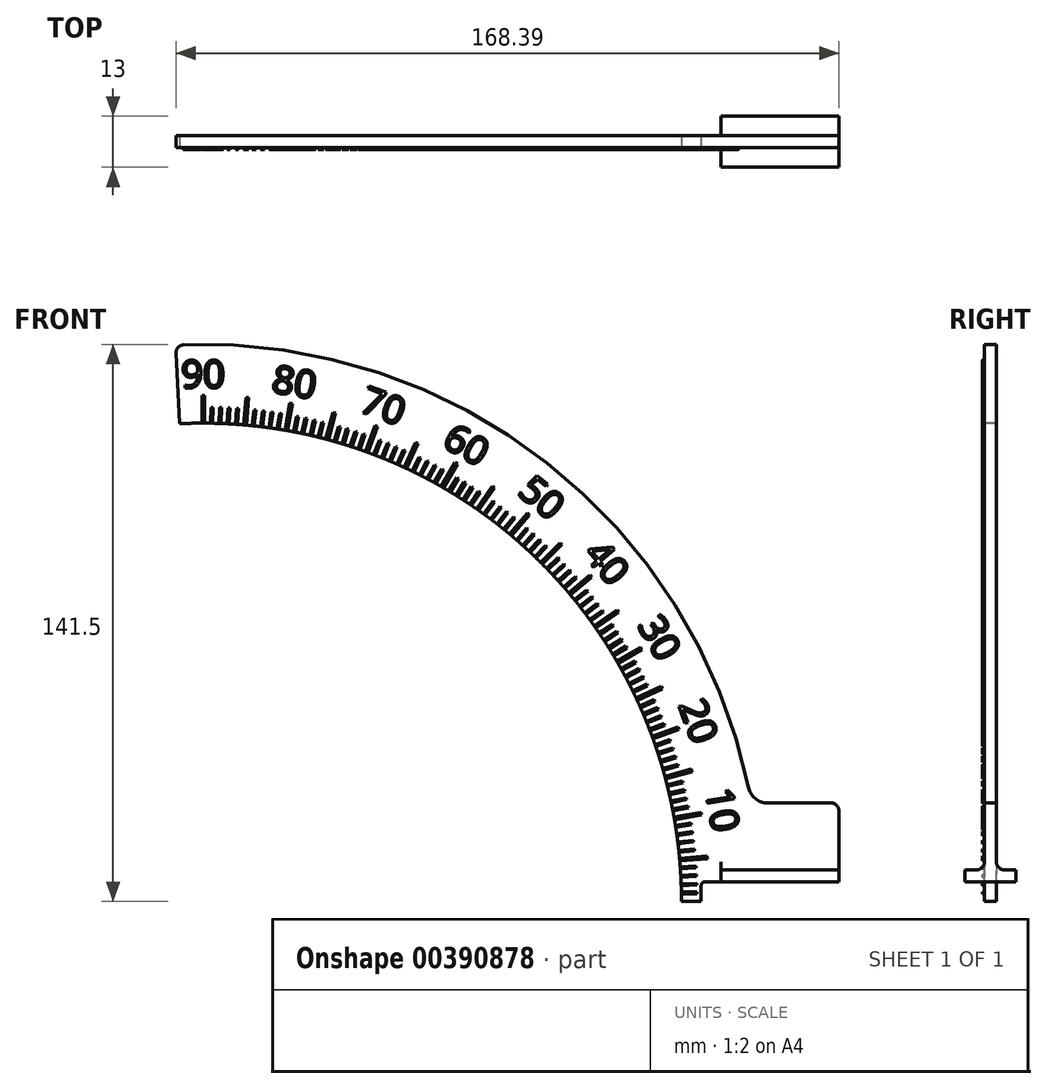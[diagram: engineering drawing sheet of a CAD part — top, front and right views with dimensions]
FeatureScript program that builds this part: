
annotation { "Feature Type Name" : "Feature", "Feature Type Description" : "" }
export const myFeature = defineFeature(function(context is Context, id is Id, definition is map)
    precondition{}
    {
        {
            var Q0;
            Q0=qCreatedBy(makeId("Front.planeOp"),FACE);
            var sketch = newSketch(context, id + "F0", { "sketchPlane" : qUnion([Q0])});
            skPoint(sketch, "E0", {"position": v(121.5, 0) * mm});
            skArc(sketch, "E1", {"start": v(121.5, 0) * mm, "mid": v(85.91, 85.91) * mm, "end": v(0, 121.5) * mm});
            skPoint(sketch, "E2", {"position": v(0, 121.5) * mm});
            skArc(sketch, "E3", {"start": v(0, 121.5) * mm, "mid": v(-3, 121.46) * mm, "end": v(-6, 121.35) * mm});
            skLineSegment(sketch, "E4", {"start": v(0, 0) * mm, "end": v(-6, 121.35) * mm, "construction": true});
            skLineSegment(sketch, "E5", {"start": v(-6, 121.35) * mm, "end": v(-6.89, 139.32) * mm, "construction": true});
            skLineSegment(sketch, "E6", {"start": v(121.5, 0) * mm, "end": v(171.8, 0) * mm});
            skLineSegment(sketch, "E7", {"start": v(0, 121.5) * mm, "end": v(0, 0) * mm, "construction": true});
            skLineSegment(sketch, "E8", {"start": v(0, 121.5) * mm, "end": v(0, 128.5) * mm, "construction": true});
            skPoint(sketch, "E9", {"position": v(0, 128.5) * mm});
            skLineSegment(sketch, "E10", {"start": v(-0.35, 121.5) * mm, "end": v(-0.35, 128.5) * mm});
            skLineSegment(sketch, "E11", {"start": v(-0.35, 128.5) * mm, "end": v(0.35, 128.5) * mm});
            skLineSegment(sketch, "E12", {"start": v(0.35, 128.5) * mm, "end": v(0.35, 121.5) * mm});
            skLineSegment(sketch, "E13", {"start": v(121.5, 0) * mm, "end": v(126.5, 0) * mm});
            skLineSegment(sketch, "E14", {"start": v(126.5, 0) * mm, "end": v(126.5, 4) * mm, "construction": true});
            skLineSegment(sketch, "E15", {"start": v(127.5, 5) * mm, "end": v(161.5, 5) * mm, "construction": true});
            skLineSegment(sketch, "E16", {"start": v(161.5, 5) * mm, "end": v(161.5, 23) * mm, "construction": true});
            skLineSegment(sketch, "E17", {"start": v(159.5, 25) * mm, "end": v(143.4, 25) * mm});
            skArc(sketch, "E18", {"start": v(-4.96, 141.41) * mm, "mid": v(87.29, 111.37) * mm, "end": v(138.5, 28.98) * mm, "construction": true});
            skLineSegment(sketch, "E19", {"start": v(0, 0) * mm, "end": v(121.5, 0) * mm, "construction": true});
            skPoint(sketch, "E20", {"position": v(0, 130.5) * mm});
            skPoint(sketch, "E21.1.0", {"position": v(11.37, 130) * mm});
            skLineSegment(sketch, "E21.1.1", {"start": v(10.85, 128.04) * mm, "end": v(11.55, 127.98) * mm});
            skLineSegment(sketch, "E21.1.2", {"start": v(10.24, 121.07) * mm, "end": v(10.85, 128.04) * mm});
            skLineSegment(sketch, "E21.1.3", {"start": v(11.55, 127.98) * mm, "end": v(10.94, 121) * mm});
            skPoint(sketch, "E21.2.0", {"position": v(22.66, 128.52) * mm});
            skLineSegment(sketch, "E21.2.1", {"start": v(21.97, 126.6) * mm, "end": v(22.66, 126.49) * mm});
            skLineSegment(sketch, "E21.2.2", {"start": v(20.75, 119.71) * mm, "end": v(21.97, 126.6) * mm});
            skLineSegment(sketch, "E21.2.3", {"start": v(22.66, 126.49) * mm, "end": v(21.44, 119.6) * mm});
            skPoint(sketch, "E21.3.0", {"position": v(33.78, 126.05) * mm});
            skLineSegment(sketch, "E21.3.1", {"start": v(32.92, 124.21) * mm, "end": v(33.6, 124.03) * mm});
            skLineSegment(sketch, "E21.3.2", {"start": v(31.1, 117.45) * mm, "end": v(32.92, 124.21) * mm});
            skLineSegment(sketch, "E21.3.3", {"start": v(33.6, 124.03) * mm, "end": v(31.78, 117.27) * mm});
            skPoint(sketch, "E21.4.0", {"position": v(44.63, 122.63) * mm});
            skLineSegment(sketch, "E21.4.1", {"start": v(43.62, 120.87) * mm, "end": v(44.28, 120.63) * mm});
            skLineSegment(sketch, "E21.4.2", {"start": v(41.23, 114.3) * mm, "end": v(43.62, 120.87) * mm});
            skLineSegment(sketch, "E21.4.3", {"start": v(44.28, 120.63) * mm, "end": v(41.88, 114.05) * mm});
            skPoint(sketch, "E21.5.0", {"position": v(55.15, 118.27) * mm});
            skLineSegment(sketch, "E21.5.1", {"start": v(53.99, 116.6) * mm, "end": v(54.62, 116.31) * mm});
            skLineSegment(sketch, "E21.5.2", {"start": v(51.03, 110.26) * mm, "end": v(53.99, 116.6) * mm});
            skLineSegment(sketch, "E21.5.3", {"start": v(54.62, 116.31) * mm, "end": v(51.67, 109.97) * mm});
            skPoint(sketch, "E21.6.0", {"position": v(65.25, 113.02) * mm});
            skLineSegment(sketch, "E21.6.1", {"start": v(63.95, 111.46) * mm, "end": v(64.55, 111.1) * mm});
            skLineSegment(sketch, "E21.6.2", {"start": v(60.45, 105.4) * mm, "end": v(63.95, 111.46) * mm});
            skLineSegment(sketch, "E21.6.3", {"start": v(64.55, 111.1) * mm, "end": v(61.05, 105.05) * mm});
            skPoint(sketch, "E21.7.0", {"position": v(74.85, 106.9) * mm});
            skLineSegment(sketch, "E21.7.1", {"start": v(73.42, 105.46) * mm, "end": v(74, 105.06) * mm});
            skLineSegment(sketch, "E21.7.2", {"start": v(69.4, 99.73) * mm, "end": v(73.42, 105.46) * mm});
            skLineSegment(sketch, "E21.7.3", {"start": v(74, 105.06) * mm, "end": v(69.98, 99.33) * mm});
            skPoint(sketch, "E21.8.0", {"position": v(83.88, 99.97) * mm});
            skLineSegment(sketch, "E21.8.1", {"start": v(82.33, 98.66) * mm, "end": v(82.87, 98.21) * mm});
            skLineSegment(sketch, "E21.8.2", {"start": v(77.83, 93.3) * mm, "end": v(82.33, 98.66) * mm});
            skLineSegment(sketch, "E21.8.3", {"start": v(82.87, 98.21) * mm, "end": v(78.37, 92.85) * mm});
            skPoint(sketch, "E21.9.0", {"position": v(92.28, 92.28) * mm});
            skLineSegment(sketch, "E21.9.1", {"start": v(90.62, 91.11) * mm, "end": v(91.11, 90.62) * mm});
            skLineSegment(sketch, "E21.9.2", {"start": v(85.67, 86.16) * mm, "end": v(90.62, 91.11) * mm});
            skLineSegment(sketch, "E21.9.3", {"start": v(91.11, 90.62) * mm, "end": v(86.16, 85.67) * mm});
            skPoint(sketch, "E21.10.0", {"position": v(99.97, 83.88) * mm});
            skLineSegment(sketch, "E21.10.1", {"start": v(98.21, 82.87) * mm, "end": v(98.66, 82.33) * mm});
            skLineSegment(sketch, "E21.10.2", {"start": v(92.85, 78.37) * mm, "end": v(98.21, 82.87) * mm});
            skLineSegment(sketch, "E21.10.3", {"start": v(98.66, 82.33) * mm, "end": v(93.3, 77.83) * mm});
            skPoint(sketch, "E21.11.0", {"position": v(106.9, 74.85) * mm});
            skLineSegment(sketch, "E21.11.1", {"start": v(105.06, 74) * mm, "end": v(105.46, 73.42) * mm});
            skLineSegment(sketch, "E21.11.2", {"start": v(99.33, 69.98) * mm, "end": v(105.06, 74) * mm});
            skLineSegment(sketch, "E21.11.3", {"start": v(105.46, 73.42) * mm, "end": v(99.73, 69.4) * mm});
            skPoint(sketch, "E21.12.0", {"position": v(113.02, 65.25) * mm});
            skLineSegment(sketch, "E21.12.1", {"start": v(111.1, 64.55) * mm, "end": v(111.46, 63.95) * mm});
            skLineSegment(sketch, "E21.12.2", {"start": v(105.05, 61.05) * mm, "end": v(111.1, 64.55) * mm});
            skLineSegment(sketch, "E21.12.3", {"start": v(111.46, 63.95) * mm, "end": v(105.4, 60.45) * mm});
            skPoint(sketch, "E21.13.0", {"position": v(118.27, 55.15) * mm});
            skLineSegment(sketch, "E21.13.1", {"start": v(116.31, 54.62) * mm, "end": v(116.6, 53.99) * mm});
            skLineSegment(sketch, "E21.13.2", {"start": v(109.97, 51.67) * mm, "end": v(116.31, 54.62) * mm});
            skLineSegment(sketch, "E21.13.3", {"start": v(116.6, 53.99) * mm, "end": v(110.26, 51.03) * mm});
            skPoint(sketch, "E21.14.0", {"position": v(122.63, 44.63) * mm});
            skLineSegment(sketch, "E21.14.1", {"start": v(120.63, 44.28) * mm, "end": v(120.87, 43.62) * mm});
            skLineSegment(sketch, "E21.14.2", {"start": v(114.05, 41.88) * mm, "end": v(120.63, 44.28) * mm});
            skLineSegment(sketch, "E21.14.3", {"start": v(120.87, 43.62) * mm, "end": v(114.3, 41.23) * mm});
            skPoint(sketch, "E21.15.0", {"position": v(126.05, 33.78) * mm});
            skLineSegment(sketch, "E21.15.1", {"start": v(124.03, 33.6) * mm, "end": v(124.21, 32.92) * mm});
            skLineSegment(sketch, "E21.15.2", {"start": v(117.27, 31.78) * mm, "end": v(124.03, 33.6) * mm});
            skLineSegment(sketch, "E21.15.3", {"start": v(124.21, 32.92) * mm, "end": v(117.45, 31.1) * mm});
            skPoint(sketch, "E21.16.0", {"position": v(128.52, 22.66) * mm});
            skLineSegment(sketch, "E21.16.1", {"start": v(126.49, 22.66) * mm, "end": v(126.6, 21.97) * mm});
            skLineSegment(sketch, "E21.16.2", {"start": v(119.6, 21.44) * mm, "end": v(126.49, 22.66) * mm});
            skLineSegment(sketch, "E21.16.3", {"start": v(126.6, 21.97) * mm, "end": v(119.71, 20.75) * mm});
            skPoint(sketch, "E21.17.0", {"position": v(130, 11.37) * mm});
            skLineSegment(sketch, "E21.17.1", {"start": v(127.98, 11.55) * mm, "end": v(128.04, 10.85) * mm});
            skLineSegment(sketch, "E21.17.2", {"start": v(121, 10.94) * mm, "end": v(127.98, 11.55) * mm});
            skLineSegment(sketch, "E21.17.3", {"start": v(128.04, 10.85) * mm, "end": v(121.07, 10.24) * mm});
            skPoint(sketch, "E21.18.0", {"position": v(130.5, 0) * mm});
            skLineSegment(sketch, "E21.anchor1", {"start": v(0, 0) * mm, "end": v(0, 130.5) * mm, "construction": true});
            skLineSegment(sketch, "E21.anchor2", {"start": v(0, 0) * mm, "end": v(130.5, 0) * mm, "construction": true});
            skLineSegment(sketch, "E22", {"start": v(0.25, 121.5) * mm, "end": v(0.25, 125.5) * mm});
            skLineSegment(sketch, "E23", {"start": v(0.25, 125.5) * mm, "end": v(-0.25, 125.5) * mm});
            skLineSegment(sketch, "E24", {"start": v(-0.25, 125.5) * mm, "end": v(-0.25, 121.5) * mm});
            skPoint(sketch, "E25", {"position": v(0, 125.5) * mm});
            skPoint(sketch, "E26.1.0", {"position": v(2.2, 125.48) * mm});
            skLineSegment(sketch, "E26.1.1", {"start": v(2.44, 125.48) * mm, "end": v(1.94, 125.49) * mm});
            skLineSegment(sketch, "E26.1.2", {"start": v(2.37, 121.48) * mm, "end": v(2.44, 125.48) * mm});
            skLineSegment(sketch, "E26.1.3", {"start": v(1.94, 125.49) * mm, "end": v(1.87, 121.49) * mm});
            skPoint(sketch, "E26.2.0", {"position": v(4.38, 125.42) * mm});
            skLineSegment(sketch, "E26.2.1", {"start": v(4.63, 125.41) * mm, "end": v(4.13, 125.43) * mm});
            skLineSegment(sketch, "E26.2.2", {"start": v(4.5, 121.42) * mm, "end": v(4.63, 125.41) * mm});
            skLineSegment(sketch, "E26.2.3", {"start": v(4.13, 125.43) * mm, "end": v(4, 121.43) * mm});
            skPoint(sketch, "E26.3.0", {"position": v(6.57, 125.33) * mm});
            skLineSegment(sketch, "E26.3.1", {"start": v(6.82, 125.31) * mm, "end": v(6.32, 125.34) * mm});
            skLineSegment(sketch, "E26.3.2", {"start": v(6.6, 121.32) * mm, "end": v(6.82, 125.31) * mm});
            skLineSegment(sketch, "E26.3.3", {"start": v(6.32, 125.34) * mm, "end": v(6.1, 121.35) * mm});
            skPoint(sketch, "E26.4.0", {"position": v(8.75, 125.2) * mm});
            skLineSegment(sketch, "E26.4.1", {"start": v(9, 125.18) * mm, "end": v(8.5, 125.21) * mm});
            skLineSegment(sketch, "E26.4.2", {"start": v(8.72, 121.19) * mm, "end": v(9, 125.18) * mm});
            skLineSegment(sketch, "E26.4.3", {"start": v(8.5, 125.21) * mm, "end": v(8.23, 121.22) * mm});
            skPoint(sketch, "E26.6.0", {"position": v(13.12, 124.81) * mm});
            skLineSegment(sketch, "E26.6.1", {"start": v(13.37, 124.79) * mm, "end": v(12.87, 124.84) * mm});
            skLineSegment(sketch, "E26.6.2", {"start": v(12.95, 120.8) * mm, "end": v(13.37, 124.79) * mm});
            skLineSegment(sketch, "E26.6.3", {"start": v(12.87, 124.84) * mm, "end": v(12.45, 120.86) * mm});
            skPoint(sketch, "E26.7.0", {"position": v(15.3, 124.56) * mm});
            skLineSegment(sketch, "E26.7.1", {"start": v(15.54, 124.53) * mm, "end": v(15.05, 124.6) * mm});
            skLineSegment(sketch, "E26.7.2", {"start": v(15.06, 120.56) * mm, "end": v(15.54, 124.53) * mm});
            skLineSegment(sketch, "E26.7.3", {"start": v(15.05, 124.6) * mm, "end": v(14.56, 120.62) * mm});
            skPoint(sketch, "E26.8.0", {"position": v(17.47, 124.28) * mm});
            skLineSegment(sketch, "E26.8.1", {"start": v(17.71, 124.24) * mm, "end": v(17.22, 124.31) * mm});
            skLineSegment(sketch, "E26.8.2", {"start": v(17.16, 120.28) * mm, "end": v(17.71, 124.24) * mm});
            skLineSegment(sketch, "E26.8.3", {"start": v(17.22, 124.31) * mm, "end": v(16.66, 120.35) * mm});
            skPoint(sketch, "E26.9.0", {"position": v(19.63, 123.95) * mm});
            skLineSegment(sketch, "E26.9.1", {"start": v(19.88, 123.92) * mm, "end": v(19.39, 124) * mm});
            skLineSegment(sketch, "E26.9.2", {"start": v(19.25, 119.96) * mm, "end": v(19.88, 123.92) * mm});
            skLineSegment(sketch, "E26.9.3", {"start": v(19.39, 124) * mm, "end": v(18.76, 120.04) * mm});
            skPoint(sketch, "E26.11.0", {"position": v(23.95, 123.2) * mm});
            skLineSegment(sketch, "E26.11.1", {"start": v(24.2, 123.15) * mm, "end": v(23.7, 123.24) * mm});
            skLineSegment(sketch, "E26.11.2", {"start": v(23.43, 119.22) * mm, "end": v(24.2, 123.15) * mm});
            skLineSegment(sketch, "E26.11.3", {"start": v(23.7, 123.24) * mm, "end": v(22.94, 119.32) * mm});
            skPoint(sketch, "E26.12.0", {"position": v(26.1, 122.76) * mm});
            skLineSegment(sketch, "E26.12.1", {"start": v(26.34, 122.7) * mm, "end": v(25.85, 122.8) * mm});
            skLineSegment(sketch, "E26.12.2", {"start": v(25.5, 118.8) * mm, "end": v(26.34, 122.7) * mm});
            skLineSegment(sketch, "E26.12.3", {"start": v(25.85, 122.8) * mm, "end": v(25.02, 118.9) * mm});
            skPoint(sketch, "E26.13.0", {"position": v(28.23, 122.28) * mm});
            skLineSegment(sketch, "E26.13.1", {"start": v(28.47, 122.23) * mm, "end": v(27.99, 122.34) * mm});
            skLineSegment(sketch, "E26.13.2", {"start": v(27.58, 118.33) * mm, "end": v(28.47, 122.23) * mm});
            skLineSegment(sketch, "E26.13.3", {"start": v(27.99, 122.34) * mm, "end": v(27.09, 118.44) * mm});
            skPoint(sketch, "E26.14.0", {"position": v(30.36, 121.77) * mm});
            skLineSegment(sketch, "E26.14.1", {"start": v(30.6, 121.71) * mm, "end": v(30.12, 121.83) * mm});
            skLineSegment(sketch, "E26.14.2", {"start": v(29.64, 117.83) * mm, "end": v(30.6, 121.71) * mm});
            skLineSegment(sketch, "E26.14.3", {"start": v(30.12, 121.83) * mm, "end": v(29.15, 117.95) * mm});
            skPoint(sketch, "E26.16.0", {"position": v(34.6, 120.64) * mm});
            skLineSegment(sketch, "E26.16.1", {"start": v(34.83, 120.57) * mm, "end": v(34.35, 120.7) * mm});
            skLineSegment(sketch, "E26.16.2", {"start": v(33.73, 116.72) * mm, "end": v(34.83, 120.57) * mm});
            skLineSegment(sketch, "E26.16.3", {"start": v(34.35, 120.7) * mm, "end": v(33.25, 116.86) * mm});
            skPoint(sketch, "E26.17.0", {"position": v(36.7, 120.02) * mm});
            skLineSegment(sketch, "E26.17.1", {"start": v(36.93, 119.94) * mm, "end": v(36.45, 120.09) * mm});
            skLineSegment(sketch, "E26.17.2", {"start": v(35.76, 116.12) * mm, "end": v(36.93, 119.94) * mm});
            skLineSegment(sketch, "E26.17.3", {"start": v(36.45, 120.09) * mm, "end": v(35.28, 116.26) * mm});
            skPoint(sketch, "E26.18.0", {"position": v(38.78, 119.36) * mm});
            skLineSegment(sketch, "E26.18.1", {"start": v(39.02, 119.28) * mm, "end": v(38.54, 119.43) * mm});
            skLineSegment(sketch, "E26.18.2", {"start": v(37.78, 115.48) * mm, "end": v(39.02, 119.28) * mm});
            skLineSegment(sketch, "E26.18.3", {"start": v(38.54, 119.43) * mm, "end": v(37.3, 115.63) * mm});
            skPoint(sketch, "E26.19.0", {"position": v(40.86, 118.66) * mm});
            skLineSegment(sketch, "E26.19.1", {"start": v(41.1, 118.58) * mm, "end": v(40.62, 118.74) * mm});
            skLineSegment(sketch, "E26.19.2", {"start": v(39.8, 114.8) * mm, "end": v(41.1, 118.58) * mm});
            skLineSegment(sketch, "E26.19.3", {"start": v(40.62, 118.74) * mm, "end": v(39.32, 114.96) * mm});
            skPoint(sketch, "E26.21.0", {"position": v(44.98, 117.16) * mm});
            skLineSegment(sketch, "E26.21.1", {"start": v(45.2, 117.07) * mm, "end": v(44.74, 117.25) * mm});
            skLineSegment(sketch, "E26.21.2", {"start": v(43.78, 113.34) * mm, "end": v(45.2, 117.07) * mm});
            skLineSegment(sketch, "E26.21.3", {"start": v(44.74, 117.25) * mm, "end": v(43.3, 113.52) * mm});
            skPoint(sketch, "E26.22.0", {"position": v(47.01, 116.36) * mm});
            skLineSegment(sketch, "E26.22.1", {"start": v(47.24, 116.27) * mm, "end": v(46.78, 116.46) * mm});
            skLineSegment(sketch, "E26.22.2", {"start": v(45.75, 112.56) * mm, "end": v(47.24, 116.27) * mm});
            skLineSegment(sketch, "E26.22.3", {"start": v(46.78, 116.46) * mm, "end": v(45.28, 112.75) * mm});
            skPoint(sketch, "E26.23.0", {"position": v(49.04, 115.52) * mm});
            skLineSegment(sketch, "E26.23.1", {"start": v(49.27, 115.43) * mm, "end": v(48.8, 115.62) * mm});
            skLineSegment(sketch, "E26.23.2", {"start": v(47.7, 111.74) * mm, "end": v(49.27, 115.43) * mm});
            skLineSegment(sketch, "E26.23.3", {"start": v(48.8, 115.62) * mm, "end": v(47.24, 111.94) * mm});
            skPoint(sketch, "E26.24.0", {"position": v(51.05, 114.65) * mm});
            skLineSegment(sketch, "E26.24.1", {"start": v(51.27, 114.55) * mm, "end": v(50.82, 114.75) * mm});
            skLineSegment(sketch, "E26.24.2", {"start": v(49.65, 110.9) * mm, "end": v(51.27, 114.55) * mm});
            skLineSegment(sketch, "E26.24.3", {"start": v(50.82, 114.75) * mm, "end": v(49.2, 111.1) * mm});
            skPoint(sketch, "E26.26.0", {"position": v(55.02, 112.8) * mm});
            skLineSegment(sketch, "E26.26.1", {"start": v(55.24, 112.69) * mm, "end": v(54.8, 112.9) * mm});
            skLineSegment(sketch, "E26.26.2", {"start": v(53.49, 109.1) * mm, "end": v(55.24, 112.69) * mm});
            skLineSegment(sketch, "E26.26.3", {"start": v(54.8, 112.9) * mm, "end": v(53.04, 109.31) * mm});
            skPoint(sketch, "E26.27.0", {"position": v(56.98, 111.82) * mm});
            skLineSegment(sketch, "E26.27.1", {"start": v(57.2, 111.7) * mm, "end": v(56.75, 111.93) * mm});
            skLineSegment(sketch, "E26.27.2", {"start": v(55.38, 108.14) * mm, "end": v(57.2, 111.7) * mm});
            skLineSegment(sketch, "E26.27.3", {"start": v(56.75, 111.93) * mm, "end": v(54.94, 108.37) * mm});
            skPoint(sketch, "E26.28.0", {"position": v(58.92, 110.8) * mm});
            skLineSegment(sketch, "E26.28.1", {"start": v(59.14, 110.7) * mm, "end": v(58.7, 110.93) * mm});
            skLineSegment(sketch, "E26.28.2", {"start": v(57.26, 107.16) * mm, "end": v(59.14, 110.7) * mm});
            skLineSegment(sketch, "E26.28.3", {"start": v(58.7, 110.93) * mm, "end": v(56.82, 107.4) * mm});
            skPoint(sketch, "E26.29.0", {"position": v(60.84, 109.76) * mm});
            skLineSegment(sketch, "E26.29.1", {"start": v(61.06, 109.64) * mm, "end": v(60.62, 109.89) * mm});
            skLineSegment(sketch, "E26.29.2", {"start": v(59.12, 106.14) * mm, "end": v(61.06, 109.64) * mm});
            skLineSegment(sketch, "E26.29.3", {"start": v(60.62, 109.89) * mm, "end": v(58.69, 106.39) * mm});
            skPoint(sketch, "E26.31.0", {"position": v(64.64, 107.57) * mm});
            skLineSegment(sketch, "E26.31.1", {"start": v(64.85, 107.45) * mm, "end": v(64.42, 107.7) * mm});
            skLineSegment(sketch, "E26.31.2", {"start": v(62.8, 104.02) * mm, "end": v(64.85, 107.45) * mm});
            skLineSegment(sketch, "E26.31.3", {"start": v(64.42, 107.7) * mm, "end": v(62.36, 104.27) * mm});
            skPoint(sketch, "E26.32.0", {"position": v(66.5, 106.43) * mm});
            skLineSegment(sketch, "E26.32.1", {"start": v(66.72, 106.3) * mm, "end": v(66.3, 106.56) * mm});
            skLineSegment(sketch, "E26.32.2", {"start": v(64.6, 102.9) * mm, "end": v(66.72, 106.3) * mm});
            skLineSegment(sketch, "E26.32.3", {"start": v(66.3, 106.56) * mm, "end": v(64.17, 103.17) * mm});
            skPoint(sketch, "E26.33.0", {"position": v(68.35, 105.25) * mm});
            skLineSegment(sketch, "E26.33.1", {"start": v(68.56, 105.12) * mm, "end": v(68.14, 105.39) * mm});
            skLineSegment(sketch, "E26.33.2", {"start": v(66.38, 101.76) * mm, "end": v(68.56, 105.12) * mm});
            skLineSegment(sketch, "E26.33.3", {"start": v(68.14, 105.39) * mm, "end": v(65.96, 102.03) * mm});
            skPoint(sketch, "E26.34.0", {"position": v(70.18, 104.04) * mm});
            skLineSegment(sketch, "E26.34.1", {"start": v(70.39, 103.9) * mm, "end": v(69.97, 104.18) * mm});
            skLineSegment(sketch, "E26.34.2", {"start": v(68.15, 100.59) * mm, "end": v(70.39, 103.9) * mm});
            skLineSegment(sketch, "E26.34.3", {"start": v(69.97, 104.18) * mm, "end": v(67.73, 100.87) * mm});
            skPoint(sketch, "E26.36.0", {"position": v(73.77, 101.53) * mm});
            skLineSegment(sketch, "E26.36.1", {"start": v(73.97, 101.38) * mm, "end": v(73.56, 101.68) * mm});
            skLineSegment(sketch, "E26.36.2", {"start": v(71.62, 98.15) * mm, "end": v(73.97, 101.38) * mm});
            skLineSegment(sketch, "E26.36.3", {"start": v(73.56, 101.68) * mm, "end": v(71.21, 98.44) * mm});
            skPoint(sketch, "E26.37.0", {"position": v(75.53, 100.23) * mm});
            skLineSegment(sketch, "E26.37.1", {"start": v(75.73, 100.08) * mm, "end": v(75.33, 100.38) * mm});
            skLineSegment(sketch, "E26.37.2", {"start": v(73.32, 96.88) * mm, "end": v(75.73, 100.08) * mm});
            skLineSegment(sketch, "E26.37.3", {"start": v(75.33, 100.38) * mm, "end": v(72.92, 97.18) * mm});
            skPoint(sketch, "E26.38.0", {"position": v(77.27, 98.9) * mm});
            skLineSegment(sketch, "E26.38.1", {"start": v(77.46, 98.74) * mm, "end": v(77.07, 99.05) * mm});
            skLineSegment(sketch, "E26.38.2", {"start": v(75, 95.59) * mm, "end": v(77.46, 98.74) * mm});
            skLineSegment(sketch, "E26.38.3", {"start": v(77.07, 99.05) * mm, "end": v(74.6, 95.9) * mm});
            skPoint(sketch, "E26.39.0", {"position": v(78.98, 97.53) * mm});
            skLineSegment(sketch, "E26.39.1", {"start": v(79.17, 97.37) * mm, "end": v(78.79, 97.69) * mm});
            skLineSegment(sketch, "E26.39.2", {"start": v(76.66, 94.27) * mm, "end": v(79.17, 97.37) * mm});
            skLineSegment(sketch, "E26.39.3", {"start": v(78.79, 97.69) * mm, "end": v(76.27, 94.58) * mm});
            skPoint(sketch, "E26.41.0", {"position": v(82.34, 94.72) * mm});
            skLineSegment(sketch, "E26.41.1", {"start": v(82.52, 94.55) * mm, "end": v(82.15, 94.88) * mm});
            skLineSegment(sketch, "E26.41.2", {"start": v(79.9, 91.53) * mm, "end": v(82.52, 94.55) * mm});
            skLineSegment(sketch, "E26.41.3", {"start": v(82.15, 94.88) * mm, "end": v(79.52, 91.86) * mm});
            skPoint(sketch, "E26.42.0", {"position": v(83.98, 93.26) * mm});
            skLineSegment(sketch, "E26.42.1", {"start": v(84.16, 93.1) * mm, "end": v(83.8, 93.43) * mm});
            skLineSegment(sketch, "E26.42.2", {"start": v(81.48, 90.12) * mm, "end": v(84.16, 93.1) * mm});
            skLineSegment(sketch, "E26.42.3", {"start": v(83.8, 93.43) * mm, "end": v(81.11, 90.46) * mm});
            skPoint(sketch, "E26.43.0", {"position": v(85.6, 91.78) * mm});
            skLineSegment(sketch, "E26.43.1", {"start": v(85.77, 91.61) * mm, "end": v(85.4, 91.96) * mm});
            skLineSegment(sketch, "E26.43.2", {"start": v(83.05, 88.69) * mm, "end": v(85.77, 91.61) * mm});
            skLineSegment(sketch, "E26.43.3", {"start": v(85.4, 91.96) * mm, "end": v(82.68, 89.03) * mm});
            skPoint(sketch, "E26.44.0", {"position": v(87.18, 90.28) * mm});
            skLineSegment(sketch, "E26.44.1", {"start": v(87.36, 90.1) * mm, "end": v(87, 90.45) * mm});
            skLineSegment(sketch, "E26.44.2", {"start": v(84.58, 87.23) * mm, "end": v(87.36, 90.1) * mm});
            skLineSegment(sketch, "E26.44.3", {"start": v(87, 90.45) * mm, "end": v(84.22, 87.57) * mm});
            skPoint(sketch, "E26.46.0", {"position": v(90.28, 87.18) * mm});
            skLineSegment(sketch, "E26.46.1", {"start": v(90.45, 87) * mm, "end": v(90.1, 87.36) * mm});
            skLineSegment(sketch, "E26.46.2", {"start": v(87.57, 84.22) * mm, "end": v(90.45, 87) * mm});
            skLineSegment(sketch, "E26.46.3", {"start": v(90.1, 87.36) * mm, "end": v(87.23, 84.58) * mm});
            skPoint(sketch, "E26.47.0", {"position": v(91.78, 85.6) * mm});
            skLineSegment(sketch, "E26.47.1", {"start": v(91.96, 85.4) * mm, "end": v(91.61, 85.77) * mm});
            skLineSegment(sketch, "E26.47.2", {"start": v(89.03, 82.68) * mm, "end": v(91.96, 85.4) * mm});
            skLineSegment(sketch, "E26.47.3", {"start": v(91.61, 85.77) * mm, "end": v(88.69, 83.05) * mm});
            skPoint(sketch, "E26.48.0", {"position": v(93.26, 83.98) * mm});
            skLineSegment(sketch, "E26.48.1", {"start": v(93.43, 83.8) * mm, "end": v(93.1, 84.16) * mm});
            skLineSegment(sketch, "E26.48.2", {"start": v(90.46, 81.11) * mm, "end": v(93.43, 83.8) * mm});
            skLineSegment(sketch, "E26.48.3", {"start": v(93.1, 84.16) * mm, "end": v(90.12, 81.48) * mm});
            skPoint(sketch, "E26.49.0", {"position": v(94.72, 82.34) * mm});
            skLineSegment(sketch, "E26.49.1", {"start": v(94.88, 82.15) * mm, "end": v(94.55, 82.52) * mm});
            skLineSegment(sketch, "E26.49.2", {"start": v(91.86, 79.52) * mm, "end": v(94.88, 82.15) * mm});
            skLineSegment(sketch, "E26.49.3", {"start": v(94.55, 82.52) * mm, "end": v(91.53, 79.9) * mm});
            skPoint(sketch, "E26.51.0", {"position": v(97.53, 78.98) * mm});
            skLineSegment(sketch, "E26.51.1", {"start": v(97.69, 78.79) * mm, "end": v(97.37, 79.17) * mm});
            skLineSegment(sketch, "E26.51.2", {"start": v(94.58, 76.27) * mm, "end": v(97.69, 78.79) * mm});
            skLineSegment(sketch, "E26.51.3", {"start": v(97.37, 79.17) * mm, "end": v(94.27, 76.66) * mm});
            skPoint(sketch, "E26.52.0", {"position": v(98.9, 77.27) * mm});
            skLineSegment(sketch, "E26.52.1", {"start": v(99.05, 77.07) * mm, "end": v(98.74, 77.46) * mm});
            skLineSegment(sketch, "E26.52.2", {"start": v(95.9, 74.6) * mm, "end": v(99.05, 77.07) * mm});
            skLineSegment(sketch, "E26.52.3", {"start": v(98.74, 77.46) * mm, "end": v(95.59, 75) * mm});
            skPoint(sketch, "E26.53.0", {"position": v(100.23, 75.53) * mm});
            skLineSegment(sketch, "E26.53.1", {"start": v(100.38, 75.33) * mm, "end": v(100.08, 75.73) * mm});
            skLineSegment(sketch, "E26.53.2", {"start": v(97.18, 72.92) * mm, "end": v(100.38, 75.33) * mm});
            skLineSegment(sketch, "E26.53.3", {"start": v(100.08, 75.73) * mm, "end": v(96.88, 73.32) * mm});
            skPoint(sketch, "E26.54.0", {"position": v(101.53, 73.77) * mm});
            skLineSegment(sketch, "E26.54.1", {"start": v(101.68, 73.56) * mm, "end": v(101.38, 73.97) * mm});
            skLineSegment(sketch, "E26.54.2", {"start": v(98.44, 71.21) * mm, "end": v(101.68, 73.56) * mm});
            skLineSegment(sketch, "E26.54.3", {"start": v(101.38, 73.97) * mm, "end": v(98.15, 71.62) * mm});
            skPoint(sketch, "E26.56.0", {"position": v(104.04, 70.18) * mm});
            skLineSegment(sketch, "E26.56.1", {"start": v(104.18, 69.97) * mm, "end": v(103.9, 70.39) * mm});
            skLineSegment(sketch, "E26.56.2", {"start": v(100.87, 67.73) * mm, "end": v(104.18, 69.97) * mm});
            skLineSegment(sketch, "E26.56.3", {"start": v(103.9, 70.39) * mm, "end": v(100.59, 68.15) * mm});
            skPoint(sketch, "E26.57.0", {"position": v(105.25, 68.35) * mm});
            skLineSegment(sketch, "E26.57.1", {"start": v(105.39, 68.14) * mm, "end": v(105.12, 68.56) * mm});
            skLineSegment(sketch, "E26.57.2", {"start": v(102.03, 65.96) * mm, "end": v(105.39, 68.14) * mm});
            skLineSegment(sketch, "E26.57.3", {"start": v(105.12, 68.56) * mm, "end": v(101.76, 66.38) * mm});
            skPoint(sketch, "E26.58.0", {"position": v(106.43, 66.5) * mm});
            skLineSegment(sketch, "E26.58.1", {"start": v(106.56, 66.3) * mm, "end": v(106.3, 66.72) * mm});
            skLineSegment(sketch, "E26.58.2", {"start": v(103.17, 64.17) * mm, "end": v(106.56, 66.3) * mm});
            skLineSegment(sketch, "E26.58.3", {"start": v(106.3, 66.72) * mm, "end": v(102.9, 64.6) * mm});
            skPoint(sketch, "E26.59.0", {"position": v(107.57, 64.64) * mm});
            skLineSegment(sketch, "E26.59.1", {"start": v(107.7, 64.42) * mm, "end": v(107.45, 64.85) * mm});
            skLineSegment(sketch, "E26.59.2", {"start": v(104.27, 62.36) * mm, "end": v(107.7, 64.42) * mm});
            skLineSegment(sketch, "E26.59.3", {"start": v(107.45, 64.85) * mm, "end": v(104.02, 62.8) * mm});
            skPoint(sketch, "E26.61.0", {"position": v(109.76, 60.84) * mm});
            skLineSegment(sketch, "E26.61.1", {"start": v(109.89, 60.62) * mm, "end": v(109.64, 61.06) * mm});
            skLineSegment(sketch, "E26.61.2", {"start": v(106.39, 58.69) * mm, "end": v(109.89, 60.62) * mm});
            skLineSegment(sketch, "E26.61.3", {"start": v(109.64, 61.06) * mm, "end": v(106.14, 59.12) * mm});
            skPoint(sketch, "E26.62.0", {"position": v(110.8, 58.92) * mm});
            skLineSegment(sketch, "E26.62.1", {"start": v(110.93, 58.7) * mm, "end": v(110.7, 59.14) * mm});
            skLineSegment(sketch, "E26.62.2", {"start": v(107.4, 56.82) * mm, "end": v(110.93, 58.7) * mm});
            skLineSegment(sketch, "E26.62.3", {"start": v(110.7, 59.14) * mm, "end": v(107.16, 57.26) * mm});
            skPoint(sketch, "E26.63.0", {"position": v(111.82, 56.98) * mm});
            skLineSegment(sketch, "E26.63.1", {"start": v(111.93, 56.75) * mm, "end": v(111.7, 57.2) * mm});
            skLineSegment(sketch, "E26.63.2", {"start": v(108.37, 54.94) * mm, "end": v(111.93, 56.75) * mm});
            skLineSegment(sketch, "E26.63.3", {"start": v(111.7, 57.2) * mm, "end": v(108.14, 55.38) * mm});
            skPoint(sketch, "E26.64.0", {"position": v(112.8, 55.02) * mm});
            skLineSegment(sketch, "E26.64.1", {"start": v(112.9, 54.8) * mm, "end": v(112.69, 55.24) * mm});
            skLineSegment(sketch, "E26.64.2", {"start": v(109.31, 53.04) * mm, "end": v(112.9, 54.8) * mm});
            skLineSegment(sketch, "E26.64.3", {"start": v(112.69, 55.24) * mm, "end": v(109.1, 53.49) * mm});
            skPoint(sketch, "E26.66.0", {"position": v(114.65, 51.05) * mm});
            skLineSegment(sketch, "E26.66.1", {"start": v(114.75, 50.82) * mm, "end": v(114.55, 51.27) * mm});
            skLineSegment(sketch, "E26.66.2", {"start": v(111.1, 49.2) * mm, "end": v(114.75, 50.82) * mm});
            skLineSegment(sketch, "E26.66.3", {"start": v(114.55, 51.27) * mm, "end": v(110.9, 49.65) * mm});
            skPoint(sketch, "E26.67.0", {"position": v(115.52, 49.04) * mm});
            skLineSegment(sketch, "E26.67.1", {"start": v(115.62, 48.8) * mm, "end": v(115.43, 49.27) * mm});
            skLineSegment(sketch, "E26.67.2", {"start": v(111.94, 47.24) * mm, "end": v(115.62, 48.8) * mm});
            skLineSegment(sketch, "E26.67.3", {"start": v(115.43, 49.27) * mm, "end": v(111.74, 47.7) * mm});
            skPoint(sketch, "E26.68.0", {"position": v(116.36, 47.01) * mm});
            skLineSegment(sketch, "E26.68.1", {"start": v(116.46, 46.78) * mm, "end": v(116.27, 47.24) * mm});
            skLineSegment(sketch, "E26.68.2", {"start": v(112.75, 45.28) * mm, "end": v(116.46, 46.78) * mm});
            skLineSegment(sketch, "E26.68.3", {"start": v(116.27, 47.24) * mm, "end": v(112.56, 45.75) * mm});
            skPoint(sketch, "E26.69.0", {"position": v(117.16, 44.98) * mm});
            skLineSegment(sketch, "E26.69.1", {"start": v(117.25, 44.74) * mm, "end": v(117.07, 45.2) * mm});
            skLineSegment(sketch, "E26.69.2", {"start": v(113.52, 43.3) * mm, "end": v(117.25, 44.74) * mm});
            skLineSegment(sketch, "E26.69.3", {"start": v(117.07, 45.2) * mm, "end": v(113.34, 43.78) * mm});
            skPoint(sketch, "E26.71.0", {"position": v(118.66, 40.86) * mm});
            skLineSegment(sketch, "E26.71.1", {"start": v(118.74, 40.62) * mm, "end": v(118.58, 41.1) * mm});
            skLineSegment(sketch, "E26.71.2", {"start": v(114.96, 39.32) * mm, "end": v(118.74, 40.62) * mm});
            skLineSegment(sketch, "E26.71.3", {"start": v(118.58, 41.1) * mm, "end": v(114.8, 39.8) * mm});
            skPoint(sketch, "E26.72.0", {"position": v(119.36, 38.78) * mm});
            skLineSegment(sketch, "E26.72.1", {"start": v(119.43, 38.54) * mm, "end": v(119.28, 39.02) * mm});
            skLineSegment(sketch, "E26.72.2", {"start": v(115.63, 37.3) * mm, "end": v(119.43, 38.54) * mm});
            skLineSegment(sketch, "E26.72.3", {"start": v(119.28, 39.02) * mm, "end": v(115.48, 37.78) * mm});
            skPoint(sketch, "E26.73.0", {"position": v(120.02, 36.7) * mm});
            skLineSegment(sketch, "E26.73.1", {"start": v(120.09, 36.45) * mm, "end": v(119.94, 36.93) * mm});
            skLineSegment(sketch, "E26.73.2", {"start": v(116.26, 35.28) * mm, "end": v(120.09, 36.45) * mm});
            skLineSegment(sketch, "E26.73.3", {"start": v(119.94, 36.93) * mm, "end": v(116.12, 35.76) * mm});
            skPoint(sketch, "E26.74.0", {"position": v(120.64, 34.6) * mm});
            skLineSegment(sketch, "E26.74.1", {"start": v(120.7, 34.35) * mm, "end": v(120.57, 34.83) * mm});
            skLineSegment(sketch, "E26.74.2", {"start": v(116.86, 33.25) * mm, "end": v(120.7, 34.35) * mm});
            skLineSegment(sketch, "E26.74.3", {"start": v(120.57, 34.83) * mm, "end": v(116.72, 33.73) * mm});
            skPoint(sketch, "E26.76.0", {"position": v(121.77, 30.36) * mm});
            skLineSegment(sketch, "E26.76.1", {"start": v(121.83, 30.12) * mm, "end": v(121.71, 30.6) * mm});
            skLineSegment(sketch, "E26.76.2", {"start": v(117.95, 29.15) * mm, "end": v(121.83, 30.12) * mm});
            skLineSegment(sketch, "E26.76.3", {"start": v(121.71, 30.6) * mm, "end": v(117.83, 29.64) * mm});
            skPoint(sketch, "E26.77.0", {"position": v(122.28, 28.23) * mm});
            skLineSegment(sketch, "E26.77.1", {"start": v(122.34, 27.99) * mm, "end": v(122.23, 28.47) * mm});
            skLineSegment(sketch, "E26.77.2", {"start": v(118.44, 27.09) * mm, "end": v(122.34, 27.99) * mm});
            skLineSegment(sketch, "E26.77.3", {"start": v(122.23, 28.47) * mm, "end": v(118.33, 27.58) * mm});
            skPoint(sketch, "E26.78.0", {"position": v(122.76, 26.1) * mm});
            skLineSegment(sketch, "E26.78.1", {"start": v(122.8, 25.85) * mm, "end": v(122.7, 26.34) * mm});
            skLineSegment(sketch, "E26.78.2", {"start": v(118.9, 25.02) * mm, "end": v(122.8, 25.85) * mm});
            skLineSegment(sketch, "E26.78.3", {"start": v(122.7, 26.34) * mm, "end": v(118.8, 25.5) * mm});
            skPoint(sketch, "E26.79.0", {"position": v(123.2, 23.95) * mm});
            skLineSegment(sketch, "E26.79.1", {"start": v(123.24, 23.7) * mm, "end": v(123.15, 24.2) * mm});
            skLineSegment(sketch, "E26.79.2", {"start": v(119.32, 22.94) * mm, "end": v(123.24, 23.7) * mm});
            skLineSegment(sketch, "E26.79.3", {"start": v(123.15, 24.2) * mm, "end": v(119.22, 23.43) * mm});
            skPoint(sketch, "E26.81.0", {"position": v(123.95, 19.63) * mm});
            skLineSegment(sketch, "E26.81.1", {"start": v(124, 19.39) * mm, "end": v(123.92, 19.88) * mm});
            skLineSegment(sketch, "E26.81.2", {"start": v(120.04, 18.76) * mm, "end": v(124, 19.39) * mm});
            skLineSegment(sketch, "E26.81.3", {"start": v(123.92, 19.88) * mm, "end": v(119.96, 19.25) * mm});
            skPoint(sketch, "E26.82.0", {"position": v(124.28, 17.47) * mm});
            skLineSegment(sketch, "E26.82.1", {"start": v(124.31, 17.22) * mm, "end": v(124.24, 17.71) * mm});
            skLineSegment(sketch, "E26.82.2", {"start": v(120.35, 16.66) * mm, "end": v(124.31, 17.22) * mm});
            skLineSegment(sketch, "E26.82.3", {"start": v(124.24, 17.71) * mm, "end": v(120.28, 17.16) * mm});
            skPoint(sketch, "E26.83.0", {"position": v(124.56, 15.3) * mm});
            skLineSegment(sketch, "E26.83.1", {"start": v(124.6, 15.05) * mm, "end": v(124.53, 15.54) * mm});
            skLineSegment(sketch, "E26.83.2", {"start": v(120.62, 14.56) * mm, "end": v(124.6, 15.05) * mm});
            skLineSegment(sketch, "E26.83.3", {"start": v(124.53, 15.54) * mm, "end": v(120.56, 15.06) * mm});
            skPoint(sketch, "E26.84.0", {"position": v(124.81, 13.12) * mm});
            skLineSegment(sketch, "E26.84.1", {"start": v(124.84, 12.87) * mm, "end": v(124.79, 13.37) * mm});
            skLineSegment(sketch, "E26.84.2", {"start": v(120.86, 12.45) * mm, "end": v(124.84, 12.87) * mm});
            skLineSegment(sketch, "E26.84.3", {"start": v(124.79, 13.37) * mm, "end": v(120.8, 12.95) * mm});
            skPoint(sketch, "E26.86.0", {"position": v(125.2, 8.75) * mm});
            skLineSegment(sketch, "E26.86.1", {"start": v(125.21, 8.5) * mm, "end": v(125.18, 9) * mm});
            skLineSegment(sketch, "E26.86.2", {"start": v(121.22, 8.23) * mm, "end": v(125.21, 8.5) * mm});
            skLineSegment(sketch, "E26.86.3", {"start": v(125.18, 9) * mm, "end": v(121.19, 8.72) * mm});
            skLineSegment(sketch, "E26.87.1", {"start": v(125.34, 6.32) * mm, "end": v(125.31, 6.82) * mm});
            skLineSegment(sketch, "E26.87.2", {"start": v(121.35, 6.1) * mm, "end": v(125.34, 6.32) * mm});
            skLineSegment(sketch, "E26.87.3", {"start": v(125.31, 6.82) * mm, "end": v(121.32, 6.6) * mm});
            skPoint(sketch, "E26.88.0", {"position": v(125.42, 4.38) * mm});
            skLineSegment(sketch, "E26.88.1", {"start": v(125.43, 4.13) * mm, "end": v(125.41, 4.63) * mm});
            skLineSegment(sketch, "E26.88.2", {"start": v(121.43, 4) * mm, "end": v(125.43, 4.13) * mm});
            skLineSegment(sketch, "E26.88.3", {"start": v(125.41, 4.63) * mm, "end": v(121.42, 4.5) * mm});
            skPoint(sketch, "E26.89.0", {"position": v(125.48, 2.2) * mm});
            skLineSegment(sketch, "E26.89.1", {"start": v(125.49, 1.94) * mm, "end": v(125.48, 2.44) * mm});
            skLineSegment(sketch, "E26.89.2", {"start": v(121.49, 1.87) * mm, "end": v(125.49, 1.94) * mm});
            skLineSegment(sketch, "E26.89.3", {"start": v(125.48, 2.44) * mm, "end": v(121.48, 2.37) * mm});
            skPoint(sketch, "E26.90.0", {"position": v(125.5, 0) * mm});
            skLineSegment(sketch, "E26.anchor1", {"start": v(0, 0) * mm, "end": v(0, 125.5) * mm, "construction": true});
            skLineSegment(sketch, "E26.anchor2", {"start": v(0, 0) * mm, "end": v(125.5, 0) * mm, "construction": true});
            skText(sketch, "E27", { "text": "90", "fontName": "OpenSans-Regular.ttf"});
            skText(sketch, "E28", { "text": "80", "fontName": "OpenSans-Regular.ttf"});
            skText(sketch, "E29", { "text": "70\n", "fontName": "OpenSans-Regular.ttf"});
            skText(sketch, "E30", { "text": "60", "fontName": "OpenSans-Regular.ttf"});
            skText(sketch, "E31", { "text": "50", "fontName": "OpenSans-Regular.ttf"});
            skText(sketch, "E32", { "text": "40", "fontName": "OpenSans-Regular.ttf"});
            skText(sketch, "E33", { "text": "30", "fontName": "OpenSans-Regular.ttf"});
            skText(sketch, "E34", { "text": "20", "fontName": "OpenSans-Regular.ttf"});
            skText(sketch, "E35", { "text": "10", "fontName": "OpenSans-Regular.ttf"});
            skPoint(sketch, "E36.visualSharp", {"position": v(139.27, 25) * mm});
            skArc(sketch, "E36.filletArc", {"start": v(138.5, 28.98) * mm, "mid": v(140.24, 26.12) * mm, "end": v(143.4, 25) * mm, "construction": true});
            skPoint(sketch, "E37.visualSharp", {"position": v(-6.99, 141.33) * mm});
            skArc(sketch, "E37.filletArc", {"start": v(-4.96, 141.41) * mm, "mid": v(-6.36, 140.77) * mm, "end": v(-6.89, 139.32) * mm, "construction": true});
            skPoint(sketch, "E38.visualSharp", {"position": v(126.5, 5) * mm});
            skArc(sketch, "E38.filletArc", {"start": v(127.5, 5) * mm, "mid": v(126.8, 4.7) * mm, "end": v(126.5, 4) * mm, "construction": true});
            skPoint(sketch, "E39.visualSharp", {"position": v(161.5, 25) * mm});
            skArc(sketch, "E39.filletArc", {"start": v(161.5, 23) * mm, "mid": v(160.91, 24.41) * mm, "end": v(159.5, 25) * mm});
            skLineSegment(sketch, "E40", {"start": v(121.5, 0.5) * mm, "end": v(126.5, 0.5) * mm});
            const initialGuessF0  = {"E27": [-0.00563, 0.1305, 1, 0, 0.007], "E28": [0.01711, 0.1295, 0.9848, -0.17365, 0.007], "E29": [0.03934, 0.12456, 0.9397, -0.34202, 0.007], "E30": [0.06037, 0.11583, 0.86603, -0.5, 0.007], "E31": [0.07957, 0.10359, 0.76604, -0.64279, 0.007], "E32": [0.09635, 0.0882, 0.64279, -0.76604, 0.007], "E33": [0.1102, 0.07013, 0.5, -0.86603, 0.007], "E34": [0.1207, 0.04993, 0.34202, -0.9397, 0.007], "E35": [0.12754, 0.0282, 0.17365, -0.9848, 0.007]};
            skSetInitialGuess(sketch, initialGuessF0);
            skSolve(sketch);
        }
        {
            var Q0;
            Q0=qCreatedBy(makeId("Front.planeOp"),FACE);
            var sketch = newSketch(context, id + "F1", { "sketchPlane" : qUnion([Q0])});
            skArc(sketch, "E41.0", {"start": v(121.5, 0) * mm, "mid": v(85.91, 85.91) * mm, "end": v(0, 121.5) * mm});
            skArc(sketch, "E42.0", {"start": v(-4.96, 141.41) * mm, "mid": v(87.29, 111.37) * mm, "end": v(138.5, 28.98) * mm});
            skArc(sketch, "E43.0", {"start": v(-4.96, 141.41) * mm, "mid": v(-6.36, 140.77) * mm, "end": v(-6.89, 139.32) * mm});
            skLineSegment(sketch, "E44.0", {"start": v(-6, 121.35) * mm, "end": v(-6.89, 139.32) * mm});
            skArc(sketch, "E45.0", {"start": v(0, 121.5) * mm, "mid": v(-3, 121.46) * mm, "end": v(-6, 121.35) * mm});
            skLineSegment(sketch, "E46.0", {"start": v(121.5, 0) * mm, "end": v(126.5, 0) * mm});
            skLineSegment(sketch, "E47.0", {"start": v(126.5, 0) * mm, "end": v(126.5, 4) * mm});
            skArc(sketch, "E48.0", {"start": v(127.5, 5) * mm, "mid": v(126.8, 4.7) * mm, "end": v(126.5, 4) * mm});
            skLineSegment(sketch, "E49.0", {"start": v(127.5, 5) * mm, "end": v(161.5, 5) * mm});
            skLineSegment(sketch, "E50.0", {"start": v(161.5, 5) * mm, "end": v(161.5, 23) * mm});
            skArc(sketch, "E51.0", {"start": v(161.5, 23) * mm, "mid": v(160.91, 24.41) * mm, "end": v(159.5, 25) * mm});
            skLineSegment(sketch, "E52.0", {"start": v(159.5, 25) * mm, "end": v(143.4, 25) * mm});
            skArc(sketch, "E53.0", {"start": v(138.5, 28.98) * mm, "mid": v(140.24, 26.12) * mm, "end": v(143.4, 25) * mm});
            skSolve(sketch);
        }
        {
            var Q0;
            Q0=qSketchRegion(id+"F1",true);
            extrude(context, id + "F2", {"entities" : qUnion([Q0]), "oppositeDirection" : true, "depth" : 3 * mm, "offsetDistance" : 25 * mm, "symmetric" : true});
        }
        {
            var Q0;
            Q0=qSketchRegion(id+"F0",true);
            extrude(context, id + "F3", {"entities" : qUnion([Q0]), "operationType" : NewBodyOperationType.ADD, "depth" : 2 * mm, "offsetDistance" : 25 * mm});
        }
        {
            var Q0;
            Q0=qCreatedBy(makeId("Front.planeOp"),FACE);
            var sketch = newSketch(context, id + "F4", { "sketchPlane" : qUnion([Q0])});
            skLineSegment(sketch, "E54.0", {"start": v(127.5, 5) * mm, "end": v(161.5, 5) * mm});
            skLineSegment(sketch, "E55", {"start": v(131.5, 5) * mm, "end": v(131.5, 8) * mm});
            skLineSegment(sketch, "E56.0", {"start": v(161.5, 5) * mm, "end": v(161.5, 23) * mm, "construction": true});
            skLineSegment(sketch, "E57", {"start": v(131.5, 8) * mm, "end": v(161.5, 8) * mm});
            skLineSegment(sketch, "E58", {"start": v(161.5, 8) * mm, "end": v(161.5, 5) * mm});
            skLineSegment(sketch, "E59", {"start": v(131.5, 5) * mm, "end": v(161.5, 5) * mm});
            skSolve(sketch);
        }
        {
            var Q0;
            {var subQ0=sQuery(id+"F4.wireOp",EDGE,"E55");Q0=makeQuery(id+"F4.imprint","IMPRINT",FACE,{"disambiguationData":[TD([[makeQuery(id+"F4.imprint","IMPRINT",EDGE,{"derivedFrom":subQ0}),-1.0]])]});}
            extrude(context, id + "F5", {"entities" : qUnion([Q0]), "operationType" : NewBodyOperationType.ADD, "depth" : 13 * mm, "offsetDistance" : 25 * mm, "symmetric" : true});
        }
        {
            var Q0;
            Q0=makeQuery(id+"F5.boolean.opBoolean","INTERSECT",EDGE,{"derivedFrom":[makeQuery(id+"F2.opExtrude","CAP_FACE",FACE,{"disambiguationData":[OSD([sQuery(id+"F1.wireOp",EDGE,"E41.0"),sQuery(id+"F1.wireOp",EDGE,"E42.0"),sQuery(id+"F1.wireOp",EDGE,"E43.0"),sQuery(id+"F1.wireOp",EDGE,"E44.0"),sQuery(id+"F1.wireOp",EDGE,"E45.0"),sQuery(id+"F1.wireOp",EDGE,"E46.0"),sQuery(id+"F1.wireOp",EDGE,"E47.0"),sQuery(id+"F1.wireOp",EDGE,"E48.0"),sQuery(id+"F1.wireOp",EDGE,"E49.0"),sQuery(id+"F1.wireOp",EDGE,"E50.0"),sQuery(id+"F1.wireOp",EDGE,"E51.0"),sQuery(id+"F1.wireOp",EDGE,"E52.0"),sQuery(id+"F1.wireOp",EDGE,"E53.0")])],"isStart":false}),makeQuery(id+"F5.opExtrude","SWEPT_FACE",FACE,{"disambiguationData":[OSD([sQuery(id+"F4.wireOp",EDGE,"E57")])]})]});
            var Q1;
            {var subQ49=sQuery(id+"F1.wireOp",EDGE,"E53.0");var subQ50=sQuery(id+"F1.wireOp",EDGE,"E52.0");var subQ52=sQuery(id+"F1.wireOp",EDGE,"E51.0");var subQ54=sQuery(id+"F1.wireOp",EDGE,"E50.0");var subQ55=sQuery(id+"F1.wireOp",EDGE,"E49.0");var subQ57=sQuery(id+"F1.wireOp",EDGE,"E48.0");var subQ59=sQuery(id+"F1.wireOp",EDGE,"E47.0");var subQ60=sQuery(id+"F1.wireOp",EDGE,"E46.0");var subQ62=sQuery(id+"F1.wireOp",EDGE,"E44.0");var subQ64=sQuery(id+"F1.wireOp",EDGE,"E43.0");var subQ65=sQuery(id+"F1.wireOp",EDGE,"E42.0");var subQ67=sQuery(id+"F1.wireOp",EDGE,"E45.0");var subQ68=sQuery(id+"F1.wireOp",EDGE,"E41.0");Q1=makeQuery(id+"F5.boolean.opBoolean","INTERSECT",EDGE,{"derivedFrom":[makeQuery(id+"F3.boolean.opBoolean","SPLIT",FACE,{"disambiguationData":[TD([makeQuery(id+"F2.opExtrude","SWEPT_FACE",FACE,{"disambiguationData":[OSD([subQ65])]})])],"derivedFrom":makeQuery(id+"F2.opExtrude","CAP_FACE",FACE,{"disambiguationData":[OSD([subQ68,subQ65,subQ64,subQ62,subQ67,subQ60,subQ59,subQ57,subQ55,subQ54,subQ52,subQ50,subQ49])],"isStart":true})}),makeQuery(id+"F5.opExtrude","SWEPT_FACE",FACE,{"disambiguationData":[OSD([sQuery(id+"F4.wireOp",EDGE,"E57")])]})]});}
            fillet(context, id + "F6", {"entities" : qUnion([Q0, Q1]), "tangentPropagation" : true, "radius" : 2 * mm, "defaultsChanged" : true, "vertexSettings" : [], "allowEdgeOverflow" : false});
        }
    });
